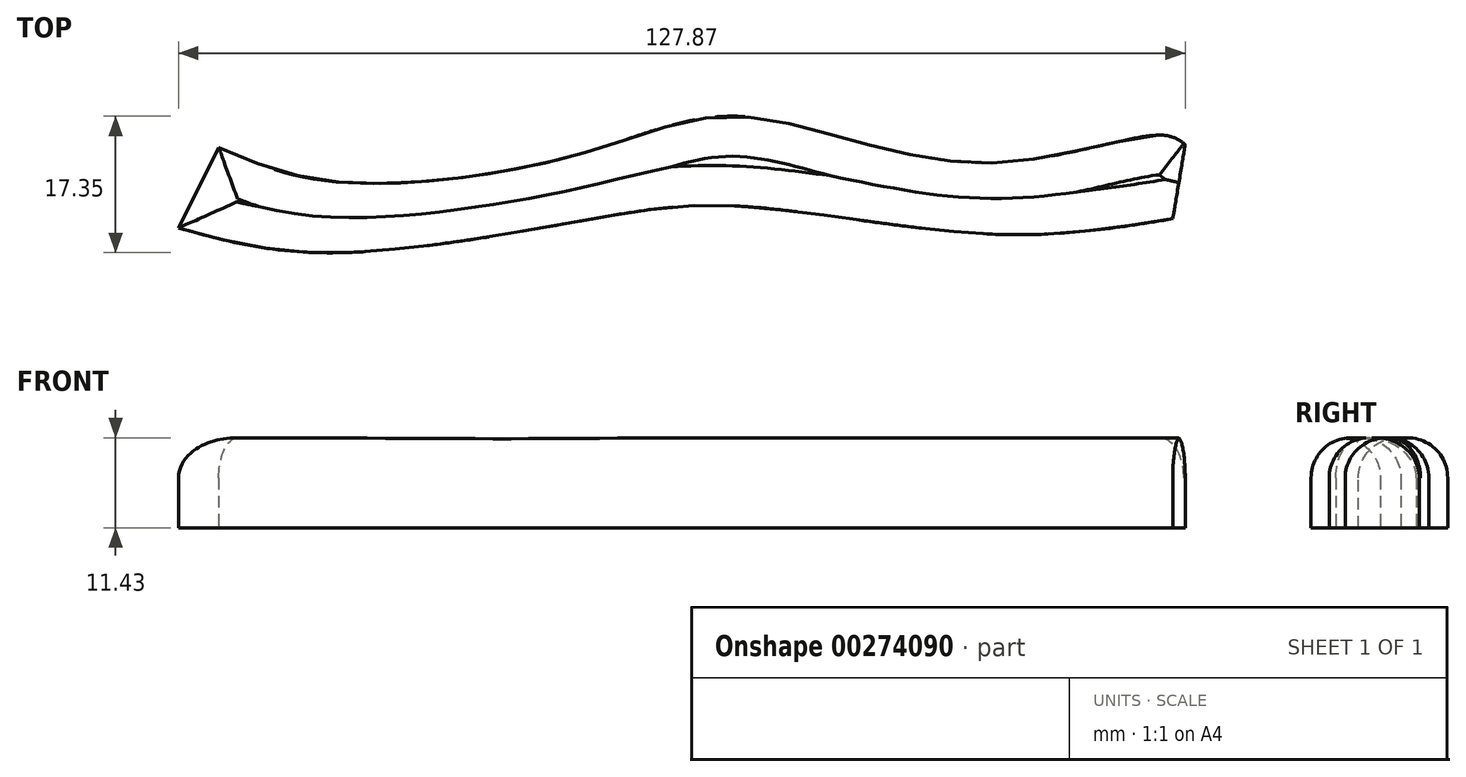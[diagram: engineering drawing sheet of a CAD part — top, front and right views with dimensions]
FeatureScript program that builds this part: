
annotation { "Feature Type Name" : "Feature", "Feature Type Description" : "" }
export const myFeature = defineFeature(function(context is Context, id is Id, definition is map)
    precondition{}
    {
        {
            var Q0;
            Q0=qCreatedBy(makeId("Top.planeOp"),FACE);
            var sketch = newSketch(context, id + "F0", { "sketchPlane" : qUnion([Q0])});
            skFitSpline(sketch, "E0", {"points": [v(-66.5, 27.14) * mm, v(-51.94, 22.82) * mm, v(-20.46, 26.36) * mm, v(0, 31.08) * mm, v(29.9, 25.18) * mm, v(53.12, 28.72) * mm, v(56.26, 27.54) * mm], "startDerivative": vector(85.06, -37.6) * mm, "endDerivative": vector(33.97, -24.82) * mm});
            skFitSpline(sketch, "E1", {"points": [v(-71.6, 16.91) * mm, v(-52.72, 13.77) * mm, v(-18.89, 18.1) * mm, v(0, 19.67) * mm, v(31.87, 16.13) * mm, v(54.7, 18.1) * mm], "startDerivative": vector(96.11, -26.7) * mm, "endDerivative": vector(110.73, 18.23) * mm});
            skLineSegment(sketch, "E2", {"start": v(-66.5, 27.14) * mm, "end": v(-71.6, 16.91) * mm});
            skLineSegment(sketch, "E3", {"start": v(56.26, 27.54) * mm, "end": v(54.7, 18.1) * mm});
            skSolve(sketch);
        }
        {
            var Q0;
            Q0=makeQuery(id+"F0.imprint","IMPRINT",FACE,{"disambiguationData":[TD([[makeQuery(id+"F0.imprint","IMPRINT",EDGE,{"derivedFrom":sQuery(id+"F0.wireOp",EDGE,"E0")}),-1.0]])]});
            extrude(context, id + "F1", {"entities" : qUnion([Q0]), "depth" : 11.43 * mm});
        }
        {
            var Q0;
            Q0=makeQuery(id+"F1.opExtrude","CAP_EDGE",EDGE,{"disambiguationData":[OSD([sQuery(id+"F0.wireOp",EDGE,"E1")])],"isStart":false});
            var Q1;
            Q1=makeQuery(id+"F1.opExtrude","CAP_EDGE",EDGE,{"disambiguationData":[OSD([sQuery(id+"F0.wireOp",EDGE,"E0")])],"isStart":false});
            var Q2;
            Q2=makeQuery(id+"F1.opExtrude","CAP_EDGE",EDGE,{"disambiguationData":[OSD([sQuery(id+"F0.wireOp",EDGE,"E2")])],"isStart":false});
            fillet(context, id + "F2", {"entities" : qUnion([Q0, Q1, Q2]), "radius" : 5.08 * mm, "tangentPropagation" : true, "allowEdgeOverflow" : false});
        }
    });
